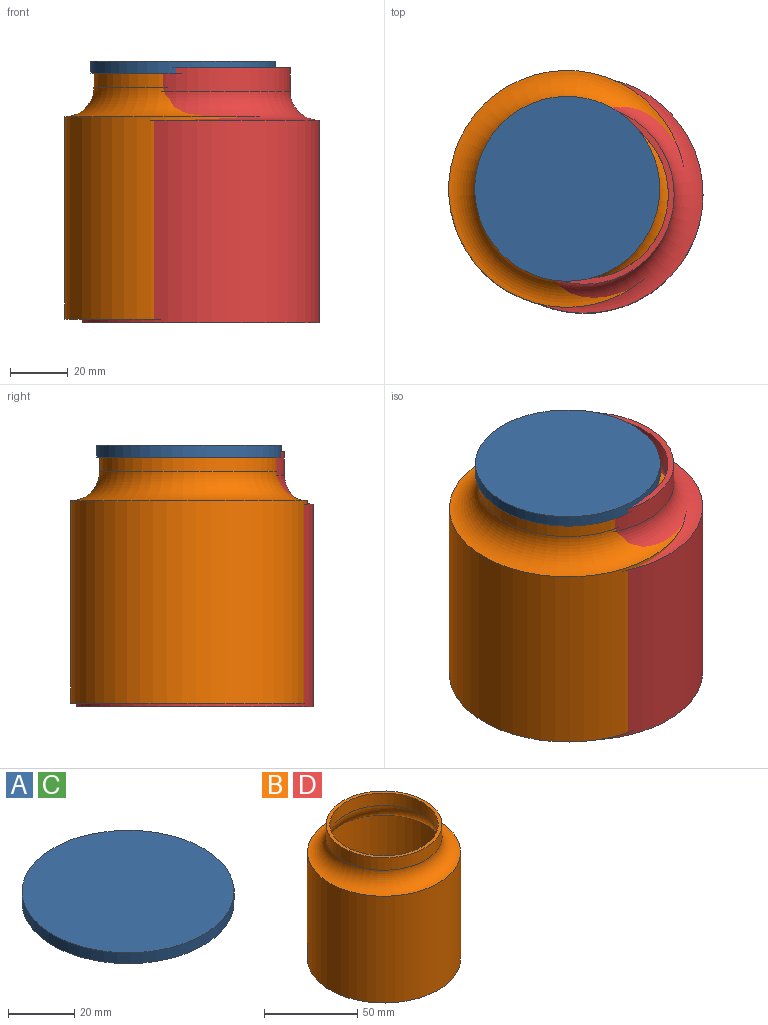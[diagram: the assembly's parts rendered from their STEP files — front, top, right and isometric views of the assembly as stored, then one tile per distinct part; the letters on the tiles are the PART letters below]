
ASSEMBLY  parts=4 mates=1
PART A: 5 faces, bbox 64x64x4 mm
  f0: cylinder r=32mm len=64mm, axis (0,0,1), area 804.2mm2, adj f1,f2
  f1: plane 64x64mm, normal (0,0,1), area 3217mm2, adj f0
  f2: plane 64x64mm, normal (0,0,-1), area 197.9mm2, adj f0,f3
  f3: cylinder r=31mm len=62mm, axis (0,0,1), area 584.3mm2, adj f2,f4
  f4: plane 62x62mm, normal (0,0,-1), area 3019.1mm2, adj f3
PART B: 9 faces, bbox 104.1x104.1x88.1 mm
  f0: plane 62x62mm, normal (0,0,1), area 377mm2, adj f4,f8
  f1: plane 82x82mm, normal (0,0,-1), area 5281mm2, adj f2
  f2: cylinder r=41mm len=82mm, axis (0,0,1), area 18032.7mm2, adj f1,f3
  f3: torus R=41mm, axis (0,0,1), area 3418.2mm2, adj f2,f4
  f4: cylinder r=31mm len=62mm, axis (0,0,1), area 1583.6mm2, adj f0,f3
  f5: plane 78x78mm, normal (0,0,1), area 4778.4mm2, adj f6
  f6: cylinder r=39mm len=78mm, axis (0,0,1), area 16214mm2, adj f5,f7
  f7: torus R=41mm, axis (0,0,1), area 3446.1mm2, adj f6,f8
  f8: cylinder r=29mm len=58mm, axis (0,0,1), area 1481.5mm2, adj f0,f7
PART C: same geometry as A
PART D: same geometry as B
PLACE A t=(-7.22,2.78,42.28)mm
PLACE B t=(-7.22,2.78,-42.85)mm
PLACE C t=(-1.35,0.6,-2)mm
PLACE D t=(-1.2,0.75,-44.07)mm
MATE fastened A.f0 <-> B.f2  axis (0,0,-1) through (-7.22,2.78,45.28)mm
